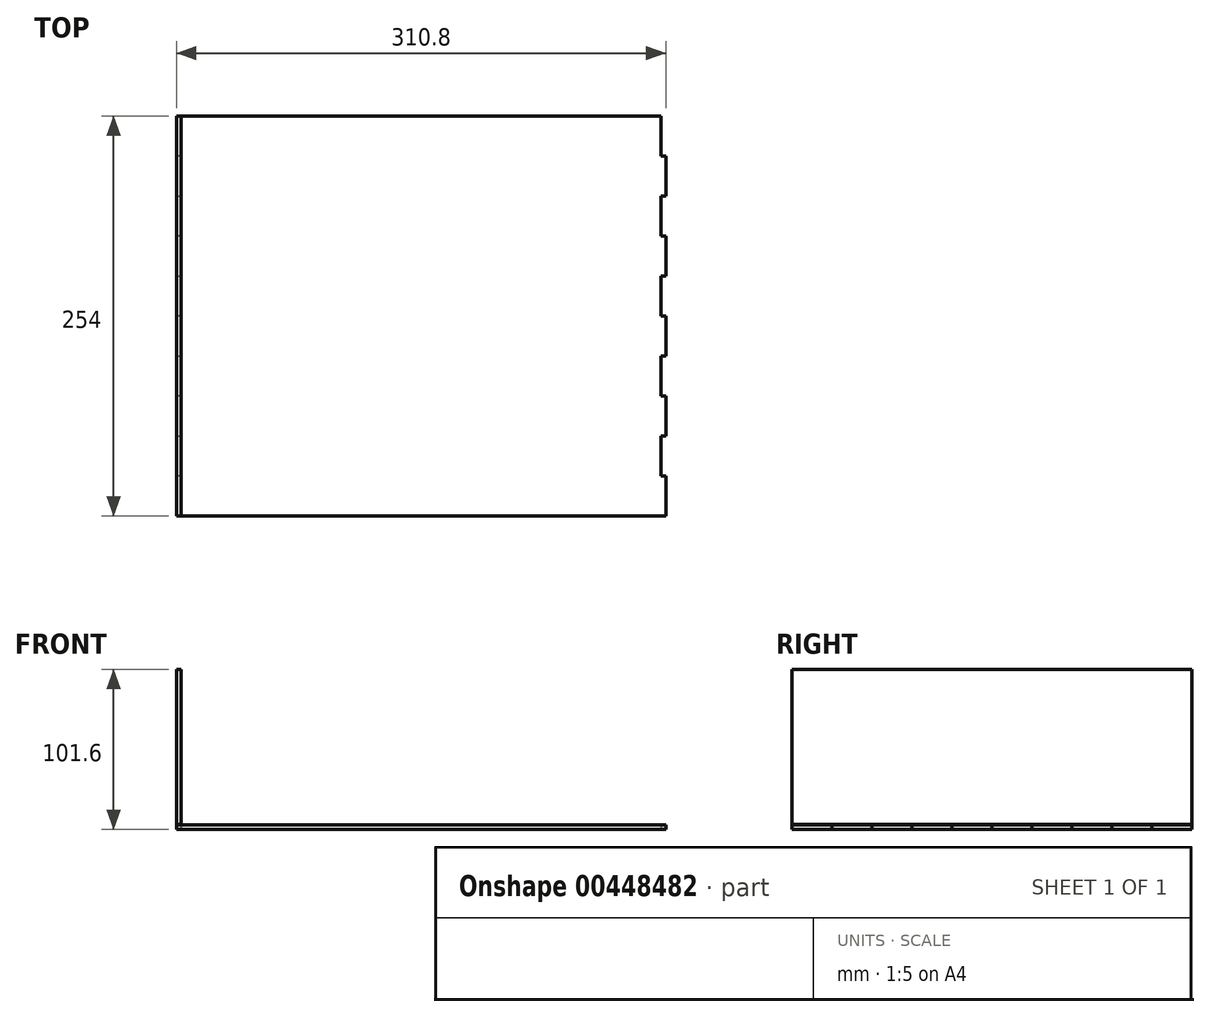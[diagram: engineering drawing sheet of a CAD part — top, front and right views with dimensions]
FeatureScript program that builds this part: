
annotation { "Feature Type Name" : "Feature", "Feature Type Description" : "" }
export const myFeature = defineFeature(function(context is Context, id is Id, definition is map)
    precondition{}
    {
        {
            var Q0;
            Q0=qCreatedBy(makeId("Top.planeOp"),FACE);
            var sketch = newSketch(context, id + "F0", { "sketchPlane" : qUnion([Q0])});
            skLineSegment(sketch, "E0.bottom", {"start": v(152.4, 127) * mm, "end": v(-152.4, 127) * mm});
            skLineSegment(sketch, "E0.top", {"start": v(152.4, -127) * mm, "end": v(-152.4, -127) * mm});
            skLineSegment(sketch, "E0.left", {"start": v(152.4, 127) * mm, "end": v(152.4, -127) * mm});
            skLineSegment(sketch, "E0.right", {"start": v(-152.4, 127) * mm, "end": v(-152.4, -127) * mm});
            skPoint(sketch, "E0.middle", {"position": v(0, 0) * mm});
            skSolve(sketch);
        }
        {
            var Q0;
            Q0=qCreatedBy(makeId("Top.planeOp"),FACE);
            var sketch = newSketch(context, id + "F1", { "sketchPlane" : qUnion([Q0])});
            skLineSegment(sketch, "E1", {"start": v(-152.4, 127) * mm, "end": v(-152.4, 101.6) * mm});
            skLineSegment(sketch, "E2", {"start": v(-152.4, 101.6) * mm, "end": v(-155.4, 101.6) * mm});
            skLineSegment(sketch, "E3", {"start": v(-155.4, 101.6) * mm, "end": v(-155.4, 76.2) * mm});
            skLineSegment(sketch, "E4", {"start": v(-155.4, 76.2) * mm, "end": v(-152.4, 76.2) * mm});
            skLineSegment(sketch, "E5.0.1.0", {"start": v(-155.4, 25.4) * mm, "end": v(-152.4, 25.4) * mm});
            skLineSegment(sketch, "E5.0.1.1", {"start": v(-152.4, 76.2) * mm, "end": v(-152.4, 50.8) * mm});
            skLineSegment(sketch, "E5.0.1.2", {"start": v(-152.4, 50.8) * mm, "end": v(-155.4, 50.8) * mm});
            skLineSegment(sketch, "E5.0.1.3", {"start": v(-155.4, 50.8) * mm, "end": v(-155.4, 25.4) * mm});
            skLineSegment(sketch, "E5.0.2.0", {"start": v(-155.4, -25.4) * mm, "end": v(-152.4, -25.4) * mm});
            skLineSegment(sketch, "E5.0.2.1", {"start": v(-152.4, 25.4) * mm, "end": v(-152.4, 0) * mm});
            skLineSegment(sketch, "E5.0.2.2", {"start": v(-152.4, 0) * mm, "end": v(-155.4, 0) * mm});
            skLineSegment(sketch, "E5.0.2.3", {"start": v(-155.4, 0) * mm, "end": v(-155.4, -25.4) * mm});
            skLineSegment(sketch, "E5.0.3.0", {"start": v(-155.4, -76.2) * mm, "end": v(-152.4, -76.2) * mm});
            skLineSegment(sketch, "E5.0.3.1", {"start": v(-152.4, -25.4) * mm, "end": v(-152.4, -50.8) * mm});
            skLineSegment(sketch, "E5.0.3.2", {"start": v(-152.4, -50.8) * mm, "end": v(-155.4, -50.8) * mm});
            skLineSegment(sketch, "E5.0.3.3", {"start": v(-155.4, -50.8) * mm, "end": v(-155.4, -76.2) * mm});
            skLineSegment(sketch, "E5.0.4.0", {"start": v(-155.4, -127) * mm, "end": v(-152.4, -127) * mm});
            skLineSegment(sketch, "E5.0.4.1", {"start": v(-152.4, -76.2) * mm, "end": v(-152.4, -101.6) * mm});
            skLineSegment(sketch, "E5.0.4.2", {"start": v(-152.4, -101.6) * mm, "end": v(-155.4, -101.6) * mm});
            skLineSegment(sketch, "E5.0.4.3", {"start": v(-155.4, -101.6) * mm, "end": v(-155.4, -127) * mm});
            skLineSegment(sketch, "E5.direction1", {"start": v(-155.4, 76.2) * mm, "end": v(-130, 76.2) * mm, "construction": true});
            skLineSegment(sketch, "E5.direction2", {"start": v(-155.4, 76.2) * mm, "end": v(-155.4, 25.4) * mm, "construction": true});
            skLineSegment(sketch, "E6", {"start": v(0, 173.84) * mm, "end": v(0, -167.77) * mm, "construction": true});
            skLineSegment(sketch, "E7.MirrorCS", {"start": v(155.4, 76.2) * mm, "end": v(152.4, 76.2) * mm});
            skLineSegment(sketch, "E8.MirrorCS", {"start": v(155.4, 25.4) * mm, "end": v(152.4, 25.4) * mm});
            skLineSegment(sketch, "E9.MirrorCS", {"start": v(155.4, -127) * mm, "end": v(152.4, -127) * mm});
            skLineSegment(sketch, "E10.MirrorCS", {"start": v(155.4, -76.2) * mm, "end": v(152.4, -76.2) * mm});
            skLineSegment(sketch, "E11.MirrorCS", {"start": v(152.4, -101.6) * mm, "end": v(155.4, -101.6) * mm});
            skLineSegment(sketch, "E12.MirrorCS", {"start": v(152.4, 0) * mm, "end": v(155.4, 0) * mm});
            skLineSegment(sketch, "E13.MirrorCS", {"start": v(155.4, -25.4) * mm, "end": v(152.4, -25.4) * mm});
            skLineSegment(sketch, "E14.MirrorCS", {"start": v(152.4, 50.8) * mm, "end": v(155.4, 50.8) * mm});
            skLineSegment(sketch, "E15.MirrorCS", {"start": v(152.4, 101.6) * mm, "end": v(155.4, 101.6) * mm});
            skLineSegment(sketch, "E16.MirrorCS", {"start": v(152.4, -50.8) * mm, "end": v(155.4, -50.8) * mm});
            skLineSegment(sketch, "E17.MirrorCS", {"start": v(155.4, 50.8) * mm, "end": v(155.4, 25.4) * mm});
            skLineSegment(sketch, "E18.MirrorCS", {"start": v(152.4, -76.2) * mm, "end": v(152.4, -101.6) * mm});
            skLineSegment(sketch, "E19.MirrorCS", {"start": v(155.4, 0) * mm, "end": v(155.4, -25.4) * mm});
            skLineSegment(sketch, "E20.MirrorCS", {"start": v(155.4, -101.6) * mm, "end": v(155.4, -127) * mm});
            skLineSegment(sketch, "E21.MirrorCS", {"start": v(152.4, 25.4) * mm, "end": v(152.4, 0) * mm});
            skLineSegment(sketch, "E22.MirrorCS", {"start": v(155.4, 76.2) * mm, "end": v(155.4, 25.4) * mm, "construction": true});
            skLineSegment(sketch, "E23.MirrorCS", {"start": v(155.4, 76.2) * mm, "end": v(130, 76.2) * mm, "construction": true});
            skLineSegment(sketch, "E24.MirrorCS", {"start": v(152.4, 76.2) * mm, "end": v(152.4, 50.8) * mm});
            skLineSegment(sketch, "E25.MirrorCS", {"start": v(152.4, 127) * mm, "end": v(152.4, 101.6) * mm});
            skLineSegment(sketch, "E26.MirrorCS", {"start": v(155.4, 101.6) * mm, "end": v(155.4, 76.2) * mm});
            skLineSegment(sketch, "E27.MirrorCS", {"start": v(152.4, -25.4) * mm, "end": v(152.4, -50.8) * mm});
            skLineSegment(sketch, "E28.MirrorCS", {"start": v(155.4, -50.8) * mm, "end": v(155.4, -76.2) * mm});
            skLineSegment(sketch, "E29", {"start": v(-152.4, 127) * mm, "end": v(152.4, 127) * mm});
            skLineSegment(sketch, "E30", {"start": v(-152.4, -127) * mm, "end": v(152.4, -127) * mm});
            skSolve(sketch);
        }
        {
            var Q0;
            Q0 = qSketchRegion(id + "F1", true);
            extrude(context, id + "F2", {"entities" : qUnion([Q0]), "depth" : 3 * mm});
        }
        {
            var Q0;
            Q0=makeQuery(id+"F2.opExtrude","SWEPT_FACE",FACE,{"disambiguationData":[OSD([sQuery(id+"F1.wireOp",EDGE,"E1")])]});
            var sketch = newSketch(context, id + "F3", { "sketchPlane" : qUnion([Q0])});
            skLineSegment(sketch, "E31.bottom", {"start": v(-127, 0) * mm, "end": v(127, 0) * mm});
            skLineSegment(sketch, "E31.top", {"start": v(-127, 101.6) * mm, "end": v(127, 101.6) * mm});
            skLineSegment(sketch, "E31.left", {"start": v(-127, 0) * mm, "end": v(-127, 101.6) * mm});
            skLineSegment(sketch, "E31.right", {"start": v(127, 0) * mm, "end": v(127, 101.6) * mm});
            skSolve(sketch);
        }
        {
            var Q0;
            Q0 = qSketchRegion(id + "F3", true);
            var Q1;
            Q1=makeQuery(id+"F2.opExtrude","SWEPT_FACE",FACE,{"disambiguationData":[OSD([sQuery(id+"F1.wireOp",EDGE,"E3")])]});
            extrude(context, id + "F4", {"entities" : qUnion([Q0]), "endBound" : BoundingType.UP_TO_SURFACE, "endBoundEntityFace" : qUnion([Q1]), "depth" : 25.4 * mm});
        }
        {
            var Q0;
            Q0=makeQuery(id+"F2.opExtrude","SWEPT_BODY",BODY,{"disambiguationData":[OSD([sQuery(id+"F1.wireOp",EDGE,"E1"),sQuery(id+"F1.wireOp",EDGE,"E2"),sQuery(id+"F1.wireOp",EDGE,"E3"),sQuery(id+"F1.wireOp",EDGE,"E4"),sQuery(id+"F1.wireOp",EDGE,"E5.0.1.0"),sQuery(id+"F1.wireOp",EDGE,"E5.0.1.1"),sQuery(id+"F1.wireOp",EDGE,"E5.0.1.2"),sQuery(id+"F1.wireOp",EDGE,"E5.0.1.3"),sQuery(id+"F1.wireOp",EDGE,"E5.0.2.0"),sQuery(id+"F1.wireOp",EDGE,"E5.0.2.1"),sQuery(id+"F1.wireOp",EDGE,"E5.0.2.2"),sQuery(id+"F1.wireOp",EDGE,"E5.0.2.3"),sQuery(id+"F1.wireOp",EDGE,"E5.0.3.0"),sQuery(id+"F1.wireOp",EDGE,"E5.0.3.1"),sQuery(id+"F1.wireOp",EDGE,"E5.0.3.2"),sQuery(id+"F1.wireOp",EDGE,"E5.0.3.3"),sQuery(id+"F1.wireOp",EDGE,"E5.0.4.0"),sQuery(id+"F1.wireOp",EDGE,"E5.0.4.1"),sQuery(id+"F1.wireOp",EDGE,"E5.0.4.2"),sQuery(id+"F1.wireOp",EDGE,"E5.0.4.3"),sQuery(id+"F1.wireOp",EDGE,"E7.MirrorCS"),sQuery(id+"F1.wireOp",EDGE,"E8.MirrorCS"),sQuery(id+"F1.wireOp",EDGE,"E9.MirrorCS"),sQuery(id+"F1.wireOp",EDGE,"E10.MirrorCS"),sQuery(id+"F1.wireOp",EDGE,"E11.MirrorCS"),sQuery(id+"F1.wireOp",EDGE,"E12.MirrorCS"),sQuery(id+"F1.wireOp",EDGE,"E13.MirrorCS"),sQuery(id+"F1.wireOp",EDGE,"E14.MirrorCS"),sQuery(id+"F1.wireOp",EDGE,"E15.MirrorCS"),sQuery(id+"F1.wireOp",EDGE,"E16.MirrorCS"),sQuery(id+"F1.wireOp",EDGE,"E17.MirrorCS"),sQuery(id+"F1.wireOp",EDGE,"E18.MirrorCS"),sQuery(id+"F1.wireOp",EDGE,"E19.MirrorCS"),sQuery(id+"F1.wireOp",EDGE,"E20.MirrorCS"),sQuery(id+"F1.wireOp",EDGE,"E21.MirrorCS"),sQuery(id+"F1.wireOp",EDGE,"E24.MirrorCS"),sQuery(id+"F1.wireOp",EDGE,"E25.MirrorCS"),sQuery(id+"F1.wireOp",EDGE,"E26.MirrorCS"),sQuery(id+"F1.wireOp",EDGE,"E27.MirrorCS"),sQuery(id+"F1.wireOp",EDGE,"E28.MirrorCS"),sQuery(id+"F1.wireOp",EDGE,"E29"),sQuery(id+"F1.wireOp",EDGE,"E30")])]});
            var Q1;
            Q1=makeQuery(id+"F4.opExtrude","SWEPT_BODY",BODY,{"disambiguationData":[OSD([sQuery(id+"F3.wireOp",EDGE,"E31.bottom"),sQuery(id+"F3.wireOp",EDGE,"E31.top"),sQuery(id+"F3.wireOp",EDGE,"E31.left"),sQuery(id+"F3.wireOp",EDGE,"E31.right")])]});
            booleanBodies(context, id + "F5", {"operationType" : BooleanOperationType.SUBTRACTION, "tools" : qUnion([Q0]), "targets" : qUnion([Q1]), "offset" : true, "offsetAll" : true, "offsetDistance" : 0.25 * mm, "keepTools" : true});
        }
    });
